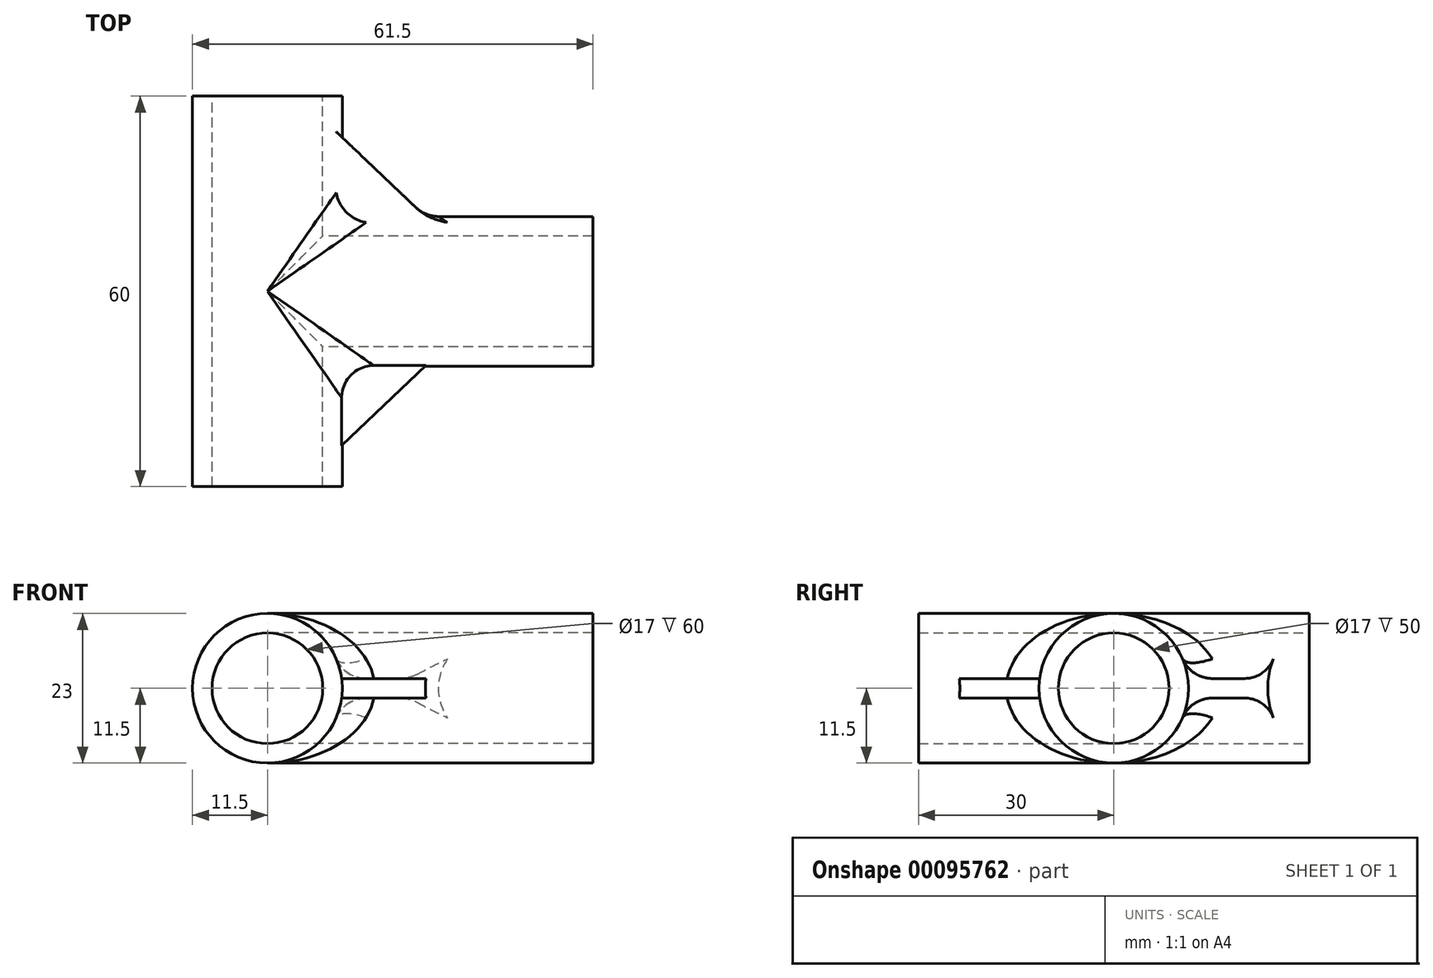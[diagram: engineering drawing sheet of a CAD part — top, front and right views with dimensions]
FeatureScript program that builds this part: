
annotation { "Feature Type Name" : "Feature", "Feature Type Description" : "" }
export const myFeature = defineFeature(function(context is Context, id is Id, definition is map)
    precondition{}
    {
        {
            var Q0;
            Q0=qCreatedBy(makeId("Front.planeOp"),FACE);
            var sketch = newSketch(context, id + "F0", { "sketchPlane" : qUnion([Q0])});
            skCircle(sketch, "E0", {"center": v(0, 0) * mm, "radius": 8.5 * mm});
            skCircle(sketch, "E1.0", {"center": v(0, 0) * mm, "radius": 11.5 * mm});
            skSolve(sketch);
        }
        {
            var Q0;
            Q0 = qSketchRegion(id + "F0", true);
            var Q1;
            Q1=makeQuery(id+"F0.imprint","IMPRINT",FACE,{"disambiguationData":[TD([[makeQuery(id+"F0.imprint","IMPRINT",EDGE,{"derivedFrom":sQuery(id+"F0.wireOp",EDGE,"E0")}),-1.0]])]});
            extrude(context, id + "F1", {"entities" : qUnion([Q0, Q1]), "endBound" : BoundingType.SYMMETRIC, "depth" : 60 * mm});
        }
        {
            var Q0;
            Q0=qCreatedBy(makeId("Right.planeOp"),FACE);
            var sketch = newSketch(context, id + "F2", { "sketchPlane" : qUnion([Q0])});
            skCircle(sketch, "E2", {"center": v(0, 0) * mm, "radius": 8.5 * mm});
            skCircle(sketch, "E3.0", {"center": v(0, 0) * mm, "radius": 11.5 * mm});
            skSolve(sketch);
        }
        {
            var Q0;
            Q0 = qSketchRegion(id + "F2", true);
            extrude(context, id + "F3", {"entities" : qUnion([Q0]), "operationType" : NewBodyOperationType.ADD, "depth" : 50 * mm});
        }
        {
            var Q0;
            Q0=qCreatedBy(makeId("Top.planeOp"),FACE);
            var sketch = newSketch(context, id + "F4", { "sketchPlane" : qUnion([Q0])});
            skLineSegment(sketch, "E4", {"start": v(10.64, 9.78) * mm, "end": v(10.64, 24.46) * mm});
            skLineSegment(sketch, "E5", {"start": v(10.64, 24.46) * mm, "end": v(26.06, 9.78) * mm});
            skLineSegment(sketch, "E6", {"start": v(26.06, 9.78) * mm, "end": v(10.64, 9.78) * mm});
            skSolve(sketch);
        }
        {
            var Q0;
            Q0=makeQuery(id+"F4.imprint","IMPRINT",FACE,{"disambiguationData":[TD([[makeQuery(id+"F4.imprint","IMPRINT",EDGE,{"derivedFrom":sQuery(id+"F4.wireOp",EDGE,"E4")}),-1.0]])]});
            extrude(context, id + "F5", {"entities" : qUnion([Q0]), "operationType" : NewBodyOperationType.ADD, "endBound" : BoundingType.SYMMETRIC, "depth" : 3 * mm});
        }
        {
            var Q0;
            Q0=makeQuery(id+"F1.opExtrude","SWEPT_BODY",BODY,{"disambiguationData":[OSD([sQuery(id+"F0.wireOp",EDGE,"E0"),sQuery(id+"F0.wireOp",EDGE,"E1.0")])]});
            var Q1;
            Q1=qCreatedBy(makeId("Front.planeOp"),FACE);
            mirror(context, id + "F6", {"operationType" : NewBodyOperationType.ADD, "entities" : qUnion([Q0]), "mirrorPlane" : qUnion([Q1])});
        }
        {
            var Q0;
            {var subQ0=makeQuery(id+"F1.opExtrude","SWEPT_FACE",FACE,{"disambiguationData":[OSD([sQuery(id+"F0.wireOp",EDGE,"E1.0")])]});var subQ1=makeQuery(id+"F3.opExtrude","SWEPT_FACE",FACE,{"disambiguationData":[OSD([sQuery(id+"F2.wireOp",EDGE,"E3.0")])]});Q0=makeQuery(id+"F5.boolean.opBoolean","SPLIT",EDGE,{"disambiguationData":[TD([makeQuery(id+"F5.opExtrude","CAP_FACE",FACE,{"disambiguationData":[OSD([sQuery(id+"F4.wireOp",EDGE,"E4"),sQuery(id+"F4.wireOp",EDGE,"E5"),sQuery(id+"F4.wireOp",EDGE,"E6")])],"isStart":true})])],"derivedFrom":makeQuery(id+"F3.boolean.opBoolean","INTERSECT",EDGE,{"disambiguationData":[OD(1.0)],"derivedFrom":[subQ0,subQ1]})});}
            var Q1;
            {var subQ0=makeQuery(id+"F1.opExtrude","SWEPT_FACE",FACE,{"disambiguationData":[OSD([sQuery(id+"F0.wireOp",EDGE,"E1.0")])]});var subQ1=makeQuery(id+"F3.opExtrude","SWEPT_FACE",FACE,{"disambiguationData":[OSD([sQuery(id+"F2.wireOp",EDGE,"E3.0")])]});Q1=makeQuery(id+"F6.boolean.opBoolean","SPLIT",EDGE,{"disambiguationData":[TD([makeQuery(id+"F6.opPattern","COPY",FACE,{"derivedFrom":makeQuery(id+"F5.opExtrude","CAP_FACE",FACE,{"disambiguationData":[OSD([sQuery(id+"F4.wireOp",EDGE,"E4"),sQuery(id+"F4.wireOp",EDGE,"E5"),sQuery(id+"F4.wireOp",EDGE,"E6")])],"isStart":true}),"instanceName":"1"})])],"derivedFrom":makeQuery(id+"F3.boolean.opBoolean","INTERSECT",EDGE,{"disambiguationData":[OD(0.0)],"derivedFrom":[subQ0,subQ1]})});}
            var Q2;
            {var subQ0=sQuery(id+"F0.wireOp",EDGE,"E1.0");Q2=makeQuery(id+"F5.boolean.opBoolean","INTERSECT",EDGE,{"derivedFrom":[makeQuery(id+"F3.boolean.opBoolean","SPLIT",FACE,{"disambiguationData":[TD([makeQuery(id+"F3.opExtrude","SWEPT_FACE",FACE,{"disambiguationData":[OSD([sQuery(id+"F2.wireOp",EDGE,"E3.0")])]})])],"derivedFrom":makeQuery(id+"F1.opExtrude","SWEPT_FACE",FACE,{"disambiguationData":[OSD([subQ0])]})}),makeQuery(id+"F5.opExtrude","CAP_FACE",FACE,{"disambiguationData":[OSD([sQuery(id+"F4.wireOp",EDGE,"E4"),sQuery(id+"F4.wireOp",EDGE,"E5"),sQuery(id+"F4.wireOp",EDGE,"E6")])],"isStart":true})]});}
            var Q3;
            {var subQ0=sQuery(id+"F2.wireOp",EDGE,"E3.0");Q3=makeQuery(id+"F5.boolean.opBoolean","INTERSECT",EDGE,{"derivedFrom":[makeQuery(id+"F3.boolean.opBoolean","SPLIT",FACE,{"disambiguationData":[TD([makeQuery(id+"F1.opExtrude","SWEPT_FACE",FACE,{"disambiguationData":[OSD([sQuery(id+"F0.wireOp",EDGE,"E1.0")])]}),makeQuery(id+"F3.opExtrude","CAP_FACE",FACE,{"disambiguationData":[OSD([sQuery(id+"F2.wireOp",EDGE,"E2"),subQ0])],"isStart":false})])],"derivedFrom":makeQuery(id+"F3.opExtrude","SWEPT_FACE",FACE,{"disambiguationData":[OSD([subQ0])]})}),makeQuery(id+"F5.opExtrude","CAP_FACE",FACE,{"disambiguationData":[OSD([sQuery(id+"F4.wireOp",EDGE,"E4"),sQuery(id+"F4.wireOp",EDGE,"E5"),sQuery(id+"F4.wireOp",EDGE,"E6")])],"isStart":true})]});}
            var Q4;
            {var subQ0=makeQuery(id+"F1.opExtrude","SWEPT_FACE",FACE,{"disambiguationData":[OSD([sQuery(id+"F0.wireOp",EDGE,"E1.0")])]});var subQ1=makeQuery(id+"F3.opExtrude","SWEPT_FACE",FACE,{"disambiguationData":[OSD([sQuery(id+"F2.wireOp",EDGE,"E3.0")])]});Q4=makeQuery(id+"F5.boolean.opBoolean","SPLIT",EDGE,{"disambiguationData":[TD([makeQuery(id+"F5.opExtrude","CAP_FACE",FACE,{"disambiguationData":[OSD([sQuery(id+"F4.wireOp",EDGE,"E4"),sQuery(id+"F4.wireOp",EDGE,"E5"),sQuery(id+"F4.wireOp",EDGE,"E6")])],"isStart":false})])],"derivedFrom":makeQuery(id+"F3.boolean.opBoolean","INTERSECT",EDGE,{"disambiguationData":[OD(1.0)],"derivedFrom":[subQ0,subQ1]})});}
            var Q5;
            {var subQ0=sQuery(id+"F2.wireOp",EDGE,"E3.0");Q5=makeQuery(id+"F5.boolean.opBoolean","INTERSECT",EDGE,{"derivedFrom":[makeQuery(id+"F3.boolean.opBoolean","SPLIT",FACE,{"disambiguationData":[TD([makeQuery(id+"F1.opExtrude","SWEPT_FACE",FACE,{"disambiguationData":[OSD([sQuery(id+"F0.wireOp",EDGE,"E1.0")])]}),makeQuery(id+"F3.opExtrude","CAP_FACE",FACE,{"disambiguationData":[OSD([sQuery(id+"F2.wireOp",EDGE,"E2"),subQ0])],"isStart":false})])],"derivedFrom":makeQuery(id+"F3.opExtrude","SWEPT_FACE",FACE,{"disambiguationData":[OSD([subQ0])]})}),makeQuery(id+"F5.opExtrude","CAP_FACE",FACE,{"disambiguationData":[OSD([sQuery(id+"F4.wireOp",EDGE,"E4"),sQuery(id+"F4.wireOp",EDGE,"E5"),sQuery(id+"F4.wireOp",EDGE,"E6")])],"isStart":false})]});}
            var Q6;
            {var subQ0=sQuery(id+"F0.wireOp",EDGE,"E1.0");Q6=makeQuery(id+"F5.boolean.opBoolean","INTERSECT",EDGE,{"derivedFrom":[makeQuery(id+"F3.boolean.opBoolean","SPLIT",FACE,{"disambiguationData":[TD([makeQuery(id+"F3.opExtrude","SWEPT_FACE",FACE,{"disambiguationData":[OSD([sQuery(id+"F2.wireOp",EDGE,"E3.0")])]})])],"derivedFrom":makeQuery(id+"F1.opExtrude","SWEPT_FACE",FACE,{"disambiguationData":[OSD([subQ0])]})}),makeQuery(id+"F5.opExtrude","CAP_FACE",FACE,{"disambiguationData":[OSD([sQuery(id+"F4.wireOp",EDGE,"E4"),sQuery(id+"F4.wireOp",EDGE,"E5"),sQuery(id+"F4.wireOp",EDGE,"E6")])],"isStart":false})]});}
            var Q7;
            {var subQ0=makeQuery(id+"F1.opExtrude","SWEPT_FACE",FACE,{"disambiguationData":[OSD([sQuery(id+"F0.wireOp",EDGE,"E1.0")])]});var subQ1=makeQuery(id+"F3.opExtrude","SWEPT_FACE",FACE,{"disambiguationData":[OSD([sQuery(id+"F2.wireOp",EDGE,"E3.0")])]});Q7=makeQuery(id+"F6.boolean.opBoolean","SPLIT",EDGE,{"disambiguationData":[TD([makeQuery(id+"F6.opPattern","COPY",FACE,{"derivedFrom":makeQuery(id+"F5.opExtrude","CAP_FACE",FACE,{"disambiguationData":[OSD([sQuery(id+"F4.wireOp",EDGE,"E4"),sQuery(id+"F4.wireOp",EDGE,"E5"),sQuery(id+"F4.wireOp",EDGE,"E6")])],"isStart":false}),"instanceName":"1"})])],"derivedFrom":makeQuery(id+"F3.boolean.opBoolean","INTERSECT",EDGE,{"disambiguationData":[OD(0.0)],"derivedFrom":[subQ0,subQ1]})});}
            var Q8;
            {var subQ0=sQuery(id+"F2.wireOp",EDGE,"E3.0");Q8=makeQuery(id+"F6.opPattern","COPY",EDGE,{"derivedFrom":makeQuery(id+"F5.boolean.opBoolean","INTERSECT",EDGE,{"derivedFrom":[makeQuery(id+"F3.boolean.opBoolean","SPLIT",FACE,{"disambiguationData":[TD([makeQuery(id+"F1.opExtrude","SWEPT_FACE",FACE,{"disambiguationData":[OSD([sQuery(id+"F0.wireOp",EDGE,"E1.0")])]}),makeQuery(id+"F3.opExtrude","CAP_FACE",FACE,{"disambiguationData":[OSD([sQuery(id+"F2.wireOp",EDGE,"E2"),subQ0])],"isStart":false})])],"derivedFrom":makeQuery(id+"F3.opExtrude","SWEPT_FACE",FACE,{"disambiguationData":[OSD([subQ0])]})}),makeQuery(id+"F5.opExtrude","CAP_FACE",FACE,{"disambiguationData":[OSD([sQuery(id+"F4.wireOp",EDGE,"E4"),sQuery(id+"F4.wireOp",EDGE,"E5"),sQuery(id+"F4.wireOp",EDGE,"E6")])],"isStart":false})]}),"instanceName":"1"});}
            var Q9;
            {var subQ0=sQuery(id+"F0.wireOp",EDGE,"E1.0");Q9=makeQuery(id+"F6.opPattern","COPY",EDGE,{"derivedFrom":makeQuery(id+"F5.boolean.opBoolean","INTERSECT",EDGE,{"derivedFrom":[makeQuery(id+"F3.boolean.opBoolean","SPLIT",FACE,{"disambiguationData":[TD([makeQuery(id+"F3.opExtrude","SWEPT_FACE",FACE,{"disambiguationData":[OSD([sQuery(id+"F2.wireOp",EDGE,"E3.0")])]})])],"derivedFrom":makeQuery(id+"F1.opExtrude","SWEPT_FACE",FACE,{"disambiguationData":[OSD([subQ0])]})}),makeQuery(id+"F5.opExtrude","CAP_FACE",FACE,{"disambiguationData":[OSD([sQuery(id+"F4.wireOp",EDGE,"E4"),sQuery(id+"F4.wireOp",EDGE,"E5"),sQuery(id+"F4.wireOp",EDGE,"E6")])],"isStart":false})]}),"instanceName":"1"});}
            var Q10;
            {var subQ0=sQuery(id+"F2.wireOp",EDGE,"E3.0");Q10=makeQuery(id+"F6.opPattern","COPY",EDGE,{"derivedFrom":makeQuery(id+"F5.boolean.opBoolean","INTERSECT",EDGE,{"derivedFrom":[makeQuery(id+"F3.boolean.opBoolean","SPLIT",FACE,{"disambiguationData":[TD([makeQuery(id+"F1.opExtrude","SWEPT_FACE",FACE,{"disambiguationData":[OSD([sQuery(id+"F0.wireOp",EDGE,"E1.0")])]}),makeQuery(id+"F3.opExtrude","CAP_FACE",FACE,{"disambiguationData":[OSD([sQuery(id+"F2.wireOp",EDGE,"E2"),subQ0])],"isStart":false})])],"derivedFrom":makeQuery(id+"F3.opExtrude","SWEPT_FACE",FACE,{"disambiguationData":[OSD([subQ0])]})}),makeQuery(id+"F5.opExtrude","CAP_FACE",FACE,{"disambiguationData":[OSD([sQuery(id+"F4.wireOp",EDGE,"E4"),sQuery(id+"F4.wireOp",EDGE,"E5"),sQuery(id+"F4.wireOp",EDGE,"E6")])],"isStart":true})]}),"instanceName":"1"});}
            var Q11;
            {var subQ0=sQuery(id+"F0.wireOp",EDGE,"E1.0");Q11=makeQuery(id+"F6.opPattern","COPY",EDGE,{"derivedFrom":makeQuery(id+"F5.boolean.opBoolean","INTERSECT",EDGE,{"derivedFrom":[makeQuery(id+"F3.boolean.opBoolean","SPLIT",FACE,{"disambiguationData":[TD([makeQuery(id+"F3.opExtrude","SWEPT_FACE",FACE,{"disambiguationData":[OSD([sQuery(id+"F2.wireOp",EDGE,"E3.0")])]})])],"derivedFrom":makeQuery(id+"F1.opExtrude","SWEPT_FACE",FACE,{"disambiguationData":[OSD([subQ0])]})}),makeQuery(id+"F5.opExtrude","CAP_FACE",FACE,{"disambiguationData":[OSD([sQuery(id+"F4.wireOp",EDGE,"E4"),sQuery(id+"F4.wireOp",EDGE,"E5"),sQuery(id+"F4.wireOp",EDGE,"E6")])],"isStart":true})]}),"instanceName":"1"});}
            var Q12;
            {var subQ0=sQuery(id+"F2.wireOp",EDGE,"E3.0");Q12=makeQuery(id+"F6.opPattern","COPY",EDGE,{"derivedFrom":makeQuery(id+"F5.boolean.opBoolean","INTERSECT",EDGE,{"derivedFrom":[makeQuery(id+"F3.boolean.opBoolean","SPLIT",FACE,{"disambiguationData":[TD([makeQuery(id+"F1.opExtrude","SWEPT_FACE",FACE,{"disambiguationData":[OSD([sQuery(id+"F0.wireOp",EDGE,"E1.0")])]}),makeQuery(id+"F3.opExtrude","CAP_FACE",FACE,{"disambiguationData":[OSD([sQuery(id+"F2.wireOp",EDGE,"E2"),subQ0])],"isStart":false})])],"derivedFrom":makeQuery(id+"F3.opExtrude","SWEPT_FACE",FACE,{"disambiguationData":[OSD([subQ0])]})}),makeQuery(id+"F5.opExtrude","SWEPT_FACE",FACE,{"disambiguationData":[OSD([sQuery(id+"F4.wireOp",EDGE,"E5")])]})]}),"instanceName":"1"});}
            var Q13;
            {var subQ0=sQuery(id+"F2.wireOp",EDGE,"E3.0");Q13=makeQuery(id+"F5.boolean.opBoolean","INTERSECT",EDGE,{"derivedFrom":[makeQuery(id+"F3.boolean.opBoolean","SPLIT",FACE,{"disambiguationData":[TD([makeQuery(id+"F1.opExtrude","SWEPT_FACE",FACE,{"disambiguationData":[OSD([sQuery(id+"F0.wireOp",EDGE,"E1.0")])]}),makeQuery(id+"F3.opExtrude","CAP_FACE",FACE,{"disambiguationData":[OSD([sQuery(id+"F2.wireOp",EDGE,"E2"),subQ0])],"isStart":false})])],"derivedFrom":makeQuery(id+"F3.opExtrude","SWEPT_FACE",FACE,{"disambiguationData":[OSD([subQ0])]})}),makeQuery(id+"F5.opExtrude","SWEPT_FACE",FACE,{"disambiguationData":[OSD([sQuery(id+"F4.wireOp",EDGE,"E5")])]})]});}
            fillet(context, id + "F7", {"entities" : qUnion([Q0, Q1, Q2, Q3, Q4, Q5, Q6, Q7, Q8, Q9, Q10, Q11, Q12, Q13]), "radius" : 5 * mm, "tangentPropagation" : true, "allowEdgeOverflow" : false});
        }
        {
            var Q0;
            Q0=makeQuery(id+"F3.opExtrude","CAP_FACE",FACE,{"disambiguationData":[OSD([sQuery(id+"F2.wireOp",EDGE,"E2"),sQuery(id+"F2.wireOp",EDGE,"E3.0")])],"isStart":false});
            var sketch = newSketch(context, id + "F8", { "sketchPlane" : qUnion([Q0])});
            skSolve(sketch);
        }
        {
            var Q0;
            Q0=makeQuery(id+"F8.imprint","IMPRINT",FACE,{"disambiguationData":[TD([[makeQuery(id+"F8.imprint","IMPRINT",EDGE,{"derivedFrom":makeQuery(id+"F3.opExtrude","CAP_EDGE",EDGE,{"disambiguationData":[OSD([sQuery(id+"F2.wireOp",EDGE,"E2")])],"isStart":false})}),1.0]])]});
            extrude(context, id + "F9", {"entities" : qUnion([Q0]), "operationType" : NewBodyOperationType.REMOVE, "oppositeDirection" : true, "depth" : 50 * mm});
        }
        {
            var Q0;
            Q0=makeQuery(id+"F1.opExtrude","CAP_FACE",FACE,{"disambiguationData":[OSD([sQuery(id+"F0.wireOp",EDGE,"E0"),sQuery(id+"F0.wireOp",EDGE,"E1.0")])],"isStart":false});
            var sketch = newSketch(context, id + "F10", { "sketchPlane" : qUnion([Q0])});
            skSolve(sketch);
        }
        {
            var Q0;
            Q0=makeQuery(id+"F10.imprint","IMPRINT",FACE,{"disambiguationData":[TD([[makeQuery(id+"F10.imprint","IMPRINT",EDGE,{"derivedFrom":makeQuery(id+"F1.opExtrude","CAP_EDGE",EDGE,{"disambiguationData":[OSD([sQuery(id+"F0.wireOp",EDGE,"E0")])],"isStart":false})}),1.0]])]});
            extrude(context, id + "F11", {"entities" : qUnion([Q0]), "operationType" : NewBodyOperationType.REMOVE, "oppositeDirection" : true, "depth" : 50 * mm});
        }
        {
            var Q0;
            Q0=makeQuery(id+"F10.imprint","IMPRINT",FACE,{"disambiguationData":[TD([[makeQuery(id+"F10.imprint","IMPRINT",EDGE,{"derivedFrom":makeQuery(id+"F1.opExtrude","CAP_EDGE",EDGE,{"disambiguationData":[OSD([sQuery(id+"F0.wireOp",EDGE,"E0")])],"isStart":false})}),1.0]])]});
            extrude(context, id + "F12", {"entities" : qUnion([Q0]), "operationType" : NewBodyOperationType.REMOVE, "oppositeDirection" : true, "depth" : 50 * mm});
        }
        {
            var Q0;
            Q0=makeQuery(id+"F3.opExtrude","CAP_FACE",FACE,{"disambiguationData":[OSD([sQuery(id+"F2.wireOp",EDGE,"E2"),sQuery(id+"F2.wireOp",EDGE,"E3.0")])],"isStart":false});
            var sketch = newSketch(context, id + "F13", { "sketchPlane" : qUnion([Q0])});
            skSolve(sketch);
        }
        {
            var Q0;
            Q0=makeQuery(id+"F13.imprint","IMPRINT",FACE,{"disambiguationData":[TD([[makeQuery(id+"F13.imprint","IMPRINT",EDGE,{"derivedFrom":makeQuery(id+"F3.opExtrude","CAP_EDGE",EDGE,{"disambiguationData":[OSD([sQuery(id+"F2.wireOp",EDGE,"E2")])],"isStart":false})}),1.0]])]});
            extrude(context, id + "F14", {"entities" : qUnion([Q0]), "operationType" : NewBodyOperationType.REMOVE, "oppositeDirection" : true, "depth" : 50 * mm});
        }
    });
